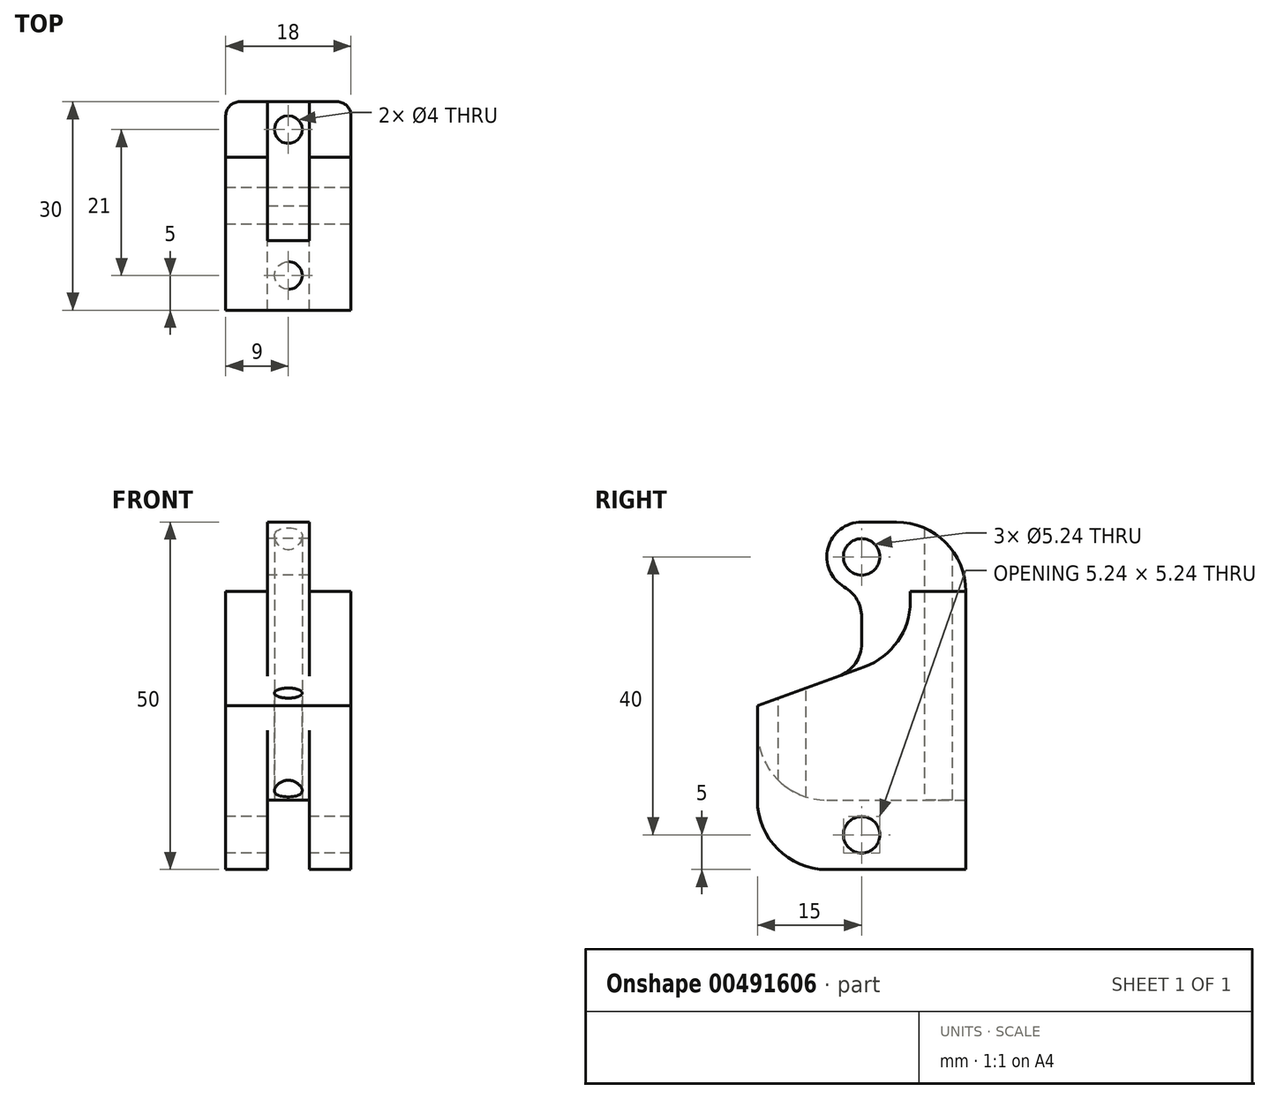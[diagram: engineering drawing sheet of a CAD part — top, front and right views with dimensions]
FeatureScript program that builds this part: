
annotation { "Feature Type Name" : "Feature", "Feature Type Description" : "" }
export const myFeature = defineFeature(function(context is Context, id is Id, definition is map)
    precondition{}
    {
        {
            var Q0;
            Q0=qCreatedBy(makeId("Front.planeOp"),FACE);
            var sketch = newSketch(context, id + "F0", { "sketchPlane" : qUnion([Q0])});
            skLineSegment(sketch, "E0.bottom", {"start": v(9, 15) * mm, "end": v(3, 15) * mm});
            skLineSegment(sketch, "E0.top", {"start": v(3, -15) * mm, "end": v(-3, -15) * mm});
            skLineSegment(sketch, "E0.left", {"start": v(9, 15) * mm, "end": v(9, -15) * mm});
            skLineSegment(sketch, "E0.right", {"start": v(-9, 15) * mm, "end": v(-9, -15) * mm});
            skPoint(sketch, "E0.middle", {"position": v(0, 0) * mm});
            skLineSegment(sketch, "E1.bottom", {"start": v(3, 25) * mm, "end": v(-3, 25) * mm});
            skLineSegment(sketch, "E1.left", {"start": v(3, 25) * mm, "end": v(3, 15) * mm});
            skLineSegment(sketch, "E1.right", {"start": v(-3, 25) * mm, "end": v(-3, 15) * mm});
            skPoint(sketch, "E1.middle", {"position": v(0, 15) * mm});
            skLineSegment(sketch, "E2.top", {"start": v(-9, -25) * mm, "end": v(-3, -25) * mm});
            skLineSegment(sketch, "E2.right", {"start": v(-3, -15) * mm, "end": v(-3, -25) * mm});
            skLineSegment(sketch, "E3.MirrorCS", {"start": v(3, -15) * mm, "end": v(3, -25) * mm});
            skLineSegment(sketch, "E4.MirrorCS", {"start": v(9, -25) * mm, "end": v(3, -25) * mm});
            skLineSegment(sketch, "E5.MirrorCS", {"start": v(9, -15) * mm, "end": v(9, -25) * mm});
            skLineSegment(sketch, "E6.trimOffspring", {"start": v(-3, 15) * mm, "end": v(-9, 15) * mm});
            skLineSegment(sketch, "E7", {"start": v(-9, -15) * mm, "end": v(-9, -25) * mm});
            skSolve(sketch);
        }
        {
            var Q0;
            Q0=makeQuery(id+"F0.imprint","IMPRINT",FACE,{"disambiguationData":[TD([[makeQuery(id+"F0.imprint","IMPRINT",EDGE,{"derivedFrom":sQuery(id+"F0.wireOp",EDGE,"E0.bottom")}),1.0]])]});
            extrude(context, id + "F1", {"entities" : qUnion([Q0]), "depth" : 30 * mm, "symmetric" : true});
        }
        {
            var Q0;
            Q0=makeQuery(id+"F1.opExtrude","SWEPT_FACE",FACE,{"disambiguationData":[OSD([sQuery(id+"F0.wireOp",EDGE,"E1.right")])]});
            var sketch = newSketch(context, id + "F2", { "sketchPlane" : qUnion([Q0])});
            skLineSegment(sketch, "E8", {"start": v(0, 15) * mm, "end": v(0, 25) * mm});
            skCircle(sketch, "E9", {"center": v(0, 20) * mm, "radius": 2.62 * mm});
            skSolve(sketch);
        }
        {
            var Q0;
            Q0=qSketchRegion(id+"F2",true);
            extrude(context, id + "F3", {"entities" : qUnion([Q0]), "operationType" : NewBodyOperationType.REMOVE, "oppositeDirection" : true, "depth" : 6 * mm});
        }
        {
            var Q0;
            Q0=makeQuery(id+"F1.opExtrude","SWEPT_FACE",FACE,{"disambiguationData":[OSD([sQuery(id+"F0.wireOp",EDGE,"E0.right"),sQuery(id+"F0.wireOp",EDGE,"E7")])]});
            var sketch = newSketch(context, id + "F4", { "sketchPlane" : qUnion([Q0])});
            skPoint(sketch, "E10.endSnap0", {"position": v(0, -25) * mm});
            skCircle(sketch, "E11", {"center": v(0, -20) * mm, "radius": 2.62 * mm});
            skLineSegment(sketch, "E12", {"start": v(0, -25) * mm, "end": v(0, -20) * mm});
            skSolve(sketch);
        }
        {
            var Q0;
            Q0=qSketchRegion(id+"F4",true);
            extrude(context, id + "F5", {"entities" : qUnion([Q0]), "operationType" : NewBodyOperationType.REMOVE, "oppositeDirection" : true, "depth" : 18 * mm});
        }
        {
            var Q0;
            Q0=makeQuery(id+"F1.opExtrude","CAP_EDGE",EDGE,{"disambiguationData":[OSD([sQuery(id+"F0.wireOp",EDGE,"E1.bottom")])],"isStart":true});
            var Q1;
            Q1=makeQuery(id+"F1.opExtrude","CAP_EDGE",EDGE,{"disambiguationData":[OSD([sQuery(id+"F0.wireOp",EDGE,"E1.bottom")])],"isStart":false});
            var Q2;
            Q2=makeQuery(id+"F1.opExtrude","CAP_EDGE",EDGE,{"disambiguationData":[OSD([sQuery(id+"F0.wireOp",EDGE,"E4.MirrorCS")])],"isStart":false});
            var Q3;
            Q3=makeQuery(id+"F1.opExtrude","CAP_EDGE",EDGE,{"disambiguationData":[OSD([sQuery(id+"F0.wireOp",EDGE,"E2.top")])],"isStart":false});
            fillet(context, id + "F6", {"entities" : qUnion([Q0, Q1, Q2, Q3]), "radius" : 10 * mm, "tangentPropagation" : true, "allowEdgeOverflow" : false});
        }
        {
            var Q0;
            Q0=makeQuery(id+"F1.opExtrude","SWEPT_FACE",FACE,{"disambiguationData":[OSD([sQuery(id+"F0.wireOp",EDGE,"E0.left"),sQuery(id+"F0.wireOp",EDGE,"E5.MirrorCS")])]});
            var sketch = newSketch(context, id + "F7", { "sketchPlane" : qUnion([Q0])});
            skPoint(sketch, "E13.endSnap0", {"position": v(0, 15) * mm});
            skLineSegment(sketch, "E14", {"start": v(-15, 15) * mm, "end": v(-15, -1.42) * mm});
            skLineSegment(sketch, "E15", {"start": v(-15, 15) * mm, "end": v(7, 15) * mm});
            skLineSegment(sketch, "E16", {"start": v(-15, -1.42) * mm, "end": v(15, -1.42) * mm});
            skLineSegment(sketch, "E17", {"start": v(-15, -1.42) * mm, "end": v(0.42, 4.2) * mm});
            skLineSegment(sketch, "E18", {"start": v(7, 15) * mm, "end": v(7, 13.59) * mm});
            skPoint(sketch, "E19.visualSharp", {"position": v(7, 6.59) * mm});
            skArc(sketch, "E19.filletArc", {"start": v(0.42, 4.2) * mm, "mid": v(5.2, 7.85) * mm, "end": v(7, 13.59) * mm});
            skSolve(sketch);
        }
        {
            var Q0;
            Q0=makeQuery(id+"F1.opExtrude","SWEPT_FACE",FACE,{"disambiguationData":[OSD([sQuery(id+"F0.wireOp",EDGE,"E0.right"),sQuery(id+"F0.wireOp",EDGE,"E7")])]});
            var sketch = newSketch(context, id + "F8", { "sketchPlane" : qUnion([Q0])});
            skLineSegment(sketch, "E20", {"start": v(-0.42, 4.2) * mm, "end": v(15, -1.42) * mm});
            skLineSegment(sketch, "E21", {"start": v(15, -1.42) * mm, "end": v(15, 15) * mm});
            skLineSegment(sketch, "E22", {"start": v(15, -1.42) * mm, "end": v(-15, -1.42) * mm});
            skLineSegment(sketch, "E23", {"start": v(15, 15) * mm, "end": v(-7, 15) * mm});
            skLineSegment(sketch, "E24", {"start": v(-7, 15) * mm, "end": v(-7, 13.59) * mm});
            skPoint(sketch, "E25.visualSharp", {"position": v(-7, 6.59) * mm});
            skArc(sketch, "E25.filletArc", {"start": v(-7, 13.59) * mm, "mid": v(-5.2, 7.85) * mm, "end": v(-0.42, 4.2) * mm});
            skSolve(sketch);
        }
        {
            var Q0;
            Q0=makeQuery(id+"F8.imprint","IMPRINT",FACE,{"disambiguationData":[TD([[makeQuery(id+"F8.imprint","IMPRINT",EDGE,{"derivedFrom":sQuery(id+"F8.wireOp",EDGE,"E20")}),1.0]])]});
            extrude(context, id + "F9", {"entities" : qUnion([Q0]), "operationType" : NewBodyOperationType.REMOVE, "oppositeDirection" : true, "depth" : 6 * mm});
        }
        {
            var Q0;
            Q0=makeQuery(id+"F7.imprint","IMPRINT",FACE,{"disambiguationData":[TD([[makeQuery(id+"F7.imprint","IMPRINT",EDGE,{"derivedFrom":sQuery(id+"F7.wireOp",EDGE,"E14")}),1.0]])]});
            extrude(context, id + "F10", {"entities" : qUnion([Q0]), "operationType" : NewBodyOperationType.REMOVE, "oppositeDirection" : true, "depth" : 6 * mm});
        }
        {
            var Q0;
            Q0=makeQuery(id+"F1.opExtrude","CAP_EDGE",EDGE,{"disambiguationData":[OSD([sQuery(id+"F0.wireOp",EDGE,"E0.left"),sQuery(id+"F0.wireOp",EDGE,"E5.MirrorCS")])],"isStart":true});
            var Q1;
            Q1=makeQuery(id+"F1.opExtrude","CAP_EDGE",EDGE,{"disambiguationData":[OSD([sQuery(id+"F0.wireOp",EDGE,"E0.right"),sQuery(id+"F0.wireOp",EDGE,"E7")])],"isStart":true});
            fillet(context, id + "F11", {"entities" : qUnion([Q0, Q1]), "radius" : 2 * mm, "tangentPropagation" : true, "allowEdgeOverflow" : false});
        }
        {
            var Q0;
            Q0=makeQuery(id+"F9.boolean.opBoolean","MERGE",FACE,{"derivedFrom":[makeQuery(id+"F1.opExtrude","SWEPT_FACE",FACE,{"disambiguationData":[OSD([sQuery(id+"F0.wireOp",EDGE,"E1.right")])]}),makeQuery(id+"F9.opExtrude","CAP_FACE",FACE,{"disambiguationData":[OSD([sQuery(id+"F8.wireOp",EDGE,"E20"),sQuery(id+"F8.wireOp",EDGE,"E21"),sQuery(id+"F8.wireOp",EDGE,"E23"),sQuery(id+"F8.wireOp",EDGE,"E24"),sQuery(id+"F8.wireOp",EDGE,"E25.filletArc")])],"isStart":false})]});
            var sketch = newSketch(context, id + "F12", { "sketchPlane" : qUnion([Q0])});
            skLineSegment(sketch, "E26", {"start": v(0, 25) * mm, "end": v(0, 22.62) * mm});
            skCircle(sketch, "E27", {"center": v(0, 20) * mm, "radius": 5 * mm});
            skLineSegment(sketch, "E28", {"start": v(0, 20) * mm, "end": v(5, 20) * mm});
            skLineSegment(sketch, "E29", {"start": v(5, 20) * mm, "end": v(5, 2.22) * mm});
            skSolve(sketch);
        }
        {
            var Q0;
            {var subQ1=sQuery(id+"F12.wireOp",EDGE,"E29");Q0=makeQuery(id+"F12.imprint","IMPRINT",FACE,{"disambiguationData":[TD([[makeQuery(id+"F12.imprint","IMPRINT",EDGE,{"derivedFrom":subQ1}),1.0]])]});}
            extrude(context, id + "F13", {"entities" : qUnion([Q0]), "operationType" : NewBodyOperationType.REMOVE, "oppositeDirection" : true, "depth" : 6 * mm});
        }
        {
            var Q0;
            Q0=makeQuery(id+"F1.opExtrude","SWEPT_FACE",FACE,{"disambiguationData":[OSD([sQuery(id+"F0.wireOp",EDGE,"E0.top")])]});
            var sketch = newSketch(context, id + "F14", { "sketchPlane" : qUnion([Q0])});
            skSolve(sketch);
        }
        {
            var Q0;
            Q0=makeQuery(id+"F1.opExtrude","CAP_EDGE",EDGE,{"disambiguationData":[OSD([sQuery(id+"F0.wireOp",EDGE,"E0.top")])],"isStart":false});
            fillet(context, id + "F15", {"entities" : qUnion([Q0]), "radius" : 10 * mm, "tangentPropagation" : true, "allowEdgeOverflow" : false});
        }
        {
            var Q0;
            {var subQ0=sQuery(id+"F8.wireOp",EDGE,"E20");Q0=makeQuery(id+"F13.boolean.opBoolean","MERGE",FACE,{"derivedFrom":[makeQuery(id+"F9.boolean.opBoolean","COPY",FACE,{"derivedFrom":makeQuery(id+"F9.opExtrude","SWEPT_FACE",FACE,{"disambiguationData":[OSD([subQ0])]})}),makeQuery(id+"F10.boolean.opBoolean","COPY",FACE,{"derivedFrom":makeQuery(id+"F10.opExtrude","SWEPT_FACE",FACE,{"disambiguationData":[OSD([sQuery(id+"F7.wireOp",EDGE,"E17")])]})}),makeQuery(id+"F13.opExtrude","SWEPT_FACE",FACE,{"disambiguationData":[OSD([subQ0])]})]});}
            var sketch = newSketch(context, id + "F16", { "sketchPlane" : qUnion([Q0])});
            skLineSegment(sketch, "E30", {"start": v(0, -3.94) * mm, "end": v(0, -14.58) * mm});
            skSolve(sketch);
        }
        {
            var Q0;
            Q0=makeQuery(id+"F13.boolean.opBoolean","COPY",EDGE,{"derivedFrom":makeQuery(id+"F13.opExtrude","SWEPT_EDGE",EDGE,{"disambiguationData":[OSD([sQuery(id+"F12.wireOp",EDGE,"E27"),sQuery(id+"F12.wireOp",EDGE,"E28"),sQuery(id+"F12.wireOp",EDGE,"E29")])]})});
            cPlane(context, id + "F17", {"entities" : qUnion([Q0]), "cplaneType" : CPlaneType.LINE_ANGLE, "offset" : 25 * mm, "angle" : 90 * degree, "width" : 150 * mm, "height" : 150 * mm});
        }
        {
            var Q0;
            Q0=qCreatedBy(id+"F17.planeOp",FACE);
            var sketch = newSketch(context, id + "F18", { "sketchPlane" : qUnion([Q0])});
            skLineSegment(sketch, "E31", {"start": v(0, -5) * mm, "end": v(0, -15) * mm});
            skCircle(sketch, "E32", {"center": v(0, -10) * mm, "radius": 2 * mm});
            skSolve(sketch);
        }
        {
            var Q0;
            Q0=qSketchRegion(id+"F18",true);
            extrude(context, id + "F19", {"entities" : qUnion([Q0]), "operationType" : NewBodyOperationType.REMOVE, "endBound" : BoundingType.THROUGH_ALL, "oppositeDirection" : true, "depth" : 40 * mm});
        }
        {
            var Q0;
            {var subQ0=sQuery(id+"F0.wireOp",EDGE,"E0.top");Q0=makeQuery(id+"F14.imprint","IMPRINT",FACE,{"disambiguationData":[TD([[makeQuery(id+"F14.imprint","IMPRINT",EDGE,{"derivedFrom":makeQuery(id+"F1.opExtrude","CAP_EDGE",EDGE,{"disambiguationData":[OSD([subQ0])],"isStart":true})}),-1.0]])]});}
            var sketch = newSketch(context, id + "F20", { "sketchPlane" : qUnion([Q0])});
            skLineSegment(sketch, "E33", {"start": v(0, -15) * mm, "end": v(0, -11) * mm});
            skCircle(sketch, "E34", {"center": v(0, -11) * mm, "radius": 2 * mm});
            skLineSegment(sketch, "E35", {"start": v(0, -11) * mm, "end": v(0, -7.51) * mm});
            skSolve(sketch);
        }
        {
            var Q0;
            {var subQ0=sQuery(id+"F20.wireOp",EDGE,"E35");var subQ1=sQuery(id+"F20.wireOp",EDGE,"E33");var subQ2=makeQuery(id+"F20.imprint","INTERSECT",VERTEX,{"derivedFrom":[subQ1,subQ0]});Q0=makeQuery(id+"F20.imprint","IMPRINT",FACE,{"disambiguationData":[TD([[makeQuery(id+"F20.imprint","IMPRINT",EDGE,{"disambiguationData":[TD([[subQ2,1.0]])],"derivedFrom":subQ1}),1.0]])]});}
            var Q1;
            {var subQ0=sQuery(id+"F20.wireOp",EDGE,"E35");var subQ1=sQuery(id+"F20.wireOp",EDGE,"E33");var subQ2=makeQuery(id+"F20.imprint","INTERSECT",VERTEX,{"derivedFrom":[subQ1,subQ0]});Q1=makeQuery(id+"F20.imprint","IMPRINT",FACE,{"disambiguationData":[TD([[makeQuery(id+"F20.imprint","IMPRINT",EDGE,{"disambiguationData":[TD([[subQ2,1.0]])],"derivedFrom":subQ1}),-1.0]])]});}
            extrude(context, id + "F21", {"entities" : qUnion([Q0, Q1]), "operationType" : NewBodyOperationType.REMOVE, "endBound" : BoundingType.THROUGH_ALL, "oppositeDirection" : true, "depth" : 50 * mm});
        }
        {
            var Q0;
            Q0=makeQuery(id+"F10.boolean.opBoolean","MERGE",FACE,{"derivedFrom":[makeQuery(id+"F1.opExtrude","SWEPT_FACE",FACE,{"disambiguationData":[OSD([sQuery(id+"F0.wireOp",EDGE,"E1.left")])]}),makeQuery(id+"F10.opExtrude","CAP_FACE",FACE,{"disambiguationData":[OSD([sQuery(id+"F7.wireOp",EDGE,"E14"),sQuery(id+"F7.wireOp",EDGE,"E15"),sQuery(id+"F7.wireOp",EDGE,"E17"),sQuery(id+"F7.wireOp",EDGE,"E18"),sQuery(id+"F7.wireOp",EDGE,"E19.filletArc")])],"isStart":false})]});
            var sketch = newSketch(context, id + "F22", { "sketchPlane" : qUnion([Q0])});
            skArc(sketch, "E36", {"start": v(-5, 20) * mm, "mid": v(-3.54, 16.46) * mm, "end": v(0, 15) * mm});
            skLineSegment(sketch, "E37", {"start": v(0, 15) * mm, "end": v(0, 4.04) * mm});
            skLineSegment(sketch, "E38", {"start": v(0, 4.04) * mm, "end": v(-5, 2.22) * mm});
            skLineSegment(sketch, "E39", {"start": v(-5, 2.22) * mm, "end": v(-5, 20) * mm});
            skSolve(sketch);
        }
        {
            var Q0;
            Q0=makeQuery(id+"F22.imprint","IMPRINT",FACE,{"disambiguationData":[TD([[makeQuery(id+"F22.imprint","IMPRINT",EDGE,{"derivedFrom":sQuery(id+"F22.wireOp",EDGE,"E36")}),-1.0]])]});
            extrude(context, id + "F23", {"entities" : qUnion([Q0]), "operationType" : NewBodyOperationType.REMOVE, "oppositeDirection" : true, "depth" : 6 * mm});
        }
        {
            var Q0;
            Q0=makeQuery(id+"F23.boolean.opBoolean","COPY",EDGE,{"derivedFrom":makeQuery(id+"F23.opExtrude","SWEPT_EDGE",EDGE,{"disambiguationData":[OSD([sQuery(id+"F22.wireOp",EDGE,"E36"),sQuery(id+"F22.wireOp",EDGE,"E37")])]})});
            var Q1;
            Q1=makeQuery(id+"F23.boolean.opBoolean","COPY",EDGE,{"derivedFrom":makeQuery(id+"F23.opExtrude","SWEPT_EDGE",EDGE,{"disambiguationData":[OSD([sQuery(id+"F7.wireOp",EDGE,"E17"),sQuery(id+"F22.wireOp",EDGE,"E37"),sQuery(id+"F22.wireOp",EDGE,"E38")])]})});
            fillet(context, id + "F24", {"entities" : qUnion([Q0, Q1]), "radius" : 5 * mm, "tangentPropagation" : true, "allowEdgeOverflow" : false});
        }
    });
